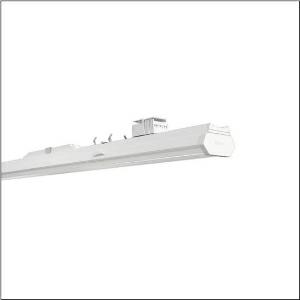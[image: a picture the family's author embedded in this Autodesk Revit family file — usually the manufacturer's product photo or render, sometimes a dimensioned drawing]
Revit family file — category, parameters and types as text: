
# Revit family: licross_r__21_protected_mo_52td11mn4a5g_25e5
name_source: partatom
category: Lighting Fixtures
units: mm (PartAtom-declared; Revit-internal decimal feet)

## family parameters
Cut with Voids When Loaded = No
Host = Face
Light Source = No
Part Type = Normal
Room Calculation Point = No
Round Connector Dimension = Use Diameter
Shared = No

## types (1)
- --- (1 x LED, 10700 lm, 60.5 W, 4000K)
    Apparent Load = 61 VA
    CIE Flux Codes = 83 94 98 100 100
    Color Rendering = 80
    Color Temperature = 4000K
    Default Elevation = 1800 mm
    Description = Licross® 21 Protected MO, luminaire insert, of sheet steel, galvanised, coil coated, white, length: 1.500mm, width: 66mm, height: 67mm, LED rated luminous flux: 10.700lm, light colour: 840, control gear: ON/OFF Multilumen, with plug, 3-pole, with phase selection, mains connection: 220..240V, AC, 50/60Hz, rated input power: 61W, internal wiring halogen-free, primary light control with lens, of plastic, primary optical cover: cover, of PMMA, light emission: direct distribution, primary light characteristic: symmetric, protection rating (complete): IP54, insulation class (complete): insulation class I (protective earthing), certification: CE, ENEC, VDE, UKCA, protection symbol: D if used in an environment with non-conductive dust loads with corresponding accessories, impact resistance: IK06, permissible ambient temperature for indoor applications: -35..+45°C, corresponds to IFS (International Featured Standards) requirements for safety and quality in the food industry, reducing of maximum allowable ambient temperature of 5°C with ceiling mounting, LABS conformity tested according to VDMA 24364:2018-05, packaging unit: 1 piece
    Height = 92 mm
    Lamp = 1 x LED
    Lamp Light Flux = 10700 lm
    Lamp Power = 60.5 W
    Lamp count = 1
    Length = 1500 mm
    Luminous efficacy = 177 lm/W
    Manufacturer = Siteco
    ModVariant = No
    Model = 52TD11MN4A5G
    Mounting Place = Ceiling
    Mounting Type = Pendant
    Number of Poles = 1
    OnlyDefault = Yes
    Power Factor = 1
    Product Name = Licross® 21 Protected MO
    Product group = luminaire insert | ceiling pendant
    ProductGroupID = 902
    Protection Class = Protection class I
    Protection Degree = IP 54
    RLX_Detail_Level = 1
    RLX_Emergency_Light_Flux = 0 lm
    RLX_Emergency_Type = 0
    RLX_Emergency_Type_DB = No
    RlxData = <blob elided: 21865 chars, md5=3e5daa94>
    Socket = socket
    Standby Power = 0 W
    System Light Flux = 10700 lm
    System Power = 61 W
    Type Comments = factory setting: luminous flux: 100 % | (A | C | E) | 140 mA
    Type Image = l_1256148.jpg
    URL = http://relux.com
    VarID = @adj_130511
    Voltage = 0 V
    Weight = 0.00 kg
    Width = 88 mm

## geometry (parser evidence)
native form markers: Blend x4, Sweep x9
no freeform markers — native parametric forms only
